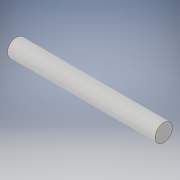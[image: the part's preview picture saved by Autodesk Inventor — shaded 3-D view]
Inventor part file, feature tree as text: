
AUTODESK INVENTOR PART (.ipt)
format: ipt  version: 2017 (Build 210142000, 142)  size: 88,576 bytes
history: native  units: in
note: dims shown in document units (in); Inventor stores cm internally (conversion verified against a paired STEP export)
features: extrude x1, sketch x1
ambient origin geometry x8: Origin, YZ Plane, XZ Plane, XY Plane, X Axis, Y Axis, Z Axis, Center Point
bodies: Solid1 (feature_tree)
feature tree (2):
  extrude  "Extrusion1"  Depth=2.11in TaperAngle=0.0deg
  sketch  "Sketch1"  dims[d0=0.25in d1=2.11in d2=0.0in]
